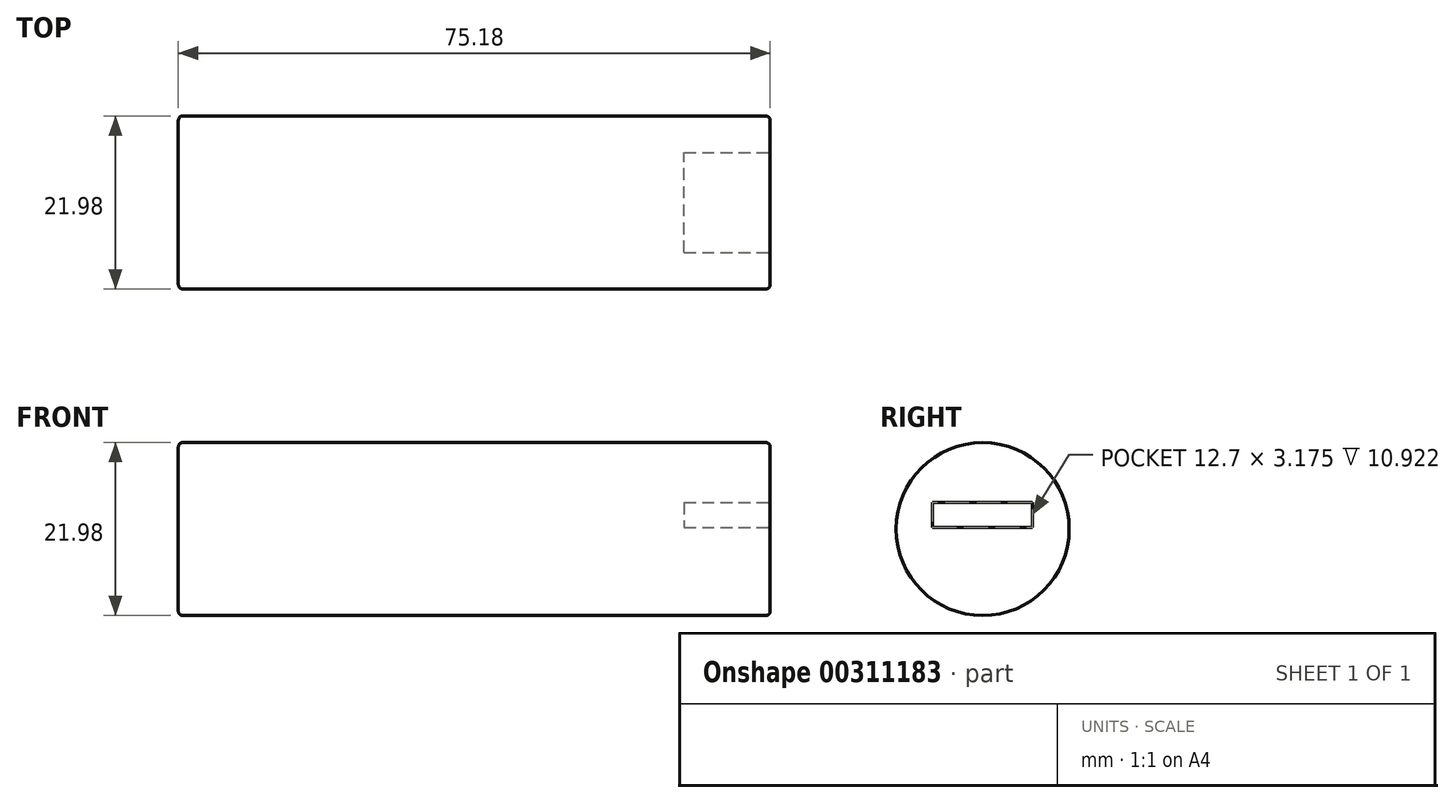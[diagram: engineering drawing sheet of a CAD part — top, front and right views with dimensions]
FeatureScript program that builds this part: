
annotation { "Feature Type Name" : "Feature", "Feature Type Description" : "" }
export const myFeature = defineFeature(function(context is Context, id is Id, definition is map)
    precondition{}
    {
        {
            var Q0;
            Q0=qCreatedBy(makeId("Right.planeOp"),FACE);
            var sketch = newSketch(context, id + "F0", { "sketchPlane" : qUnion([Q0])});
            skCircle(sketch, "E0", {"center": v(0, 0) * mm, "radius": 10.99 * mm});
            skSolve(sketch);
        }
        {
            var Q0;
            Q0=qSketchRegion(id+"F0",true);
            extrude(context, id + "F1", {"entities" : qUnion([Q0]), "endBound" : BoundingType.SYMMETRIC, "depth" : 75.18 * mm});
        }
        {
            var Q0;
            Q0=makeQuery(id+"F1.opExtrude","CAP_FACE",FACE,{"disambiguationData":[OSD([sQuery(id+"F0.wireOp",EDGE,"E0")])],"isStart":false});
            var sketch = newSketch(context, id + "F2", { "sketchPlane" : qUnion([Q0])});
            skLineSegment(sketch, "E1.bottom", {"start": v(-6.35, 3.37) * mm, "end": v(6.35, 3.37) * mm});
            skLineSegment(sketch, "E1.top", {"start": v(-6.35, 0.2) * mm, "end": v(6.35, 0.2) * mm});
            skLineSegment(sketch, "E1.left", {"start": v(-6.35, 3.37) * mm, "end": v(-6.35, 0.2) * mm});
            skLineSegment(sketch, "E1.right", {"start": v(6.35, 3.37) * mm, "end": v(6.35, 0.2) * mm});
            skLineSegment(sketch, "E2", {"start": v(0, 0) * mm, "end": v(0, 0.2) * mm, "construction": true});
            skSolve(sketch);
        }
        {
            var Q0;
            Q0=qSketchRegion(id+"F2",true);
            extrude(context, id + "F3", {"entities" : qUnion([Q0]), "operationType" : NewBodyOperationType.REMOVE, "oppositeDirection" : true, "depth" : 10.92 * mm});
        }
        {
            var Q0;
            Q0=makeQuery(id+"F1.opExtrude","CAP_EDGE",EDGE,{"disambiguationData":[OSD([sQuery(id+"F0.wireOp",EDGE,"E0")])],"isStart":false});
            var Q1;
            Q1=makeQuery(id+"F1.opExtrude","CAP_EDGE",EDGE,{"disambiguationData":[OSD([sQuery(id+"F0.wireOp",EDGE,"E0")])],"isStart":true});
            fillet(context, id + "F4", {"entities" : qUnion([Q0, Q1]), "radius" : 0.55 * mm, "tangentPropagation" : true, "allowEdgeOverflow" : false});
        }
    });
